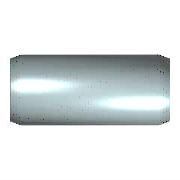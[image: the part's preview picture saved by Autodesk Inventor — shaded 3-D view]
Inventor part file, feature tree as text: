
AUTODESK INVENTOR PART (.ipt)
format: ipt  version: 2023.3 (Build 273359000, 359)  size: 116,224 bytes
history: native  units: mm (DEFAULTED — no unit token found)
features: extrude x1, chamfer x1, sketch x1
ambient origin geometry x8: Origin, YZ Plane, XZ Plane, XY Plane, X Axis, Y Axis, Z Axis, Center Point
bodies: Solid1 (feature_tree)
feature tree (3):
  extrude  "Körper"  Depth=4.0mm
  chamfer  "Skizze2"  [1 undecoded]
  sketch  "Skizze"  dims[d1=1.0mm d2=4.0mm d3=0.0mm d4=0.2mm d5=15.0deg d8=0.2mm d9=15.0deg d11=0.2mm d12=0.2mm d13=0.0mm d15=0.0mm d16=0.0mm]
note: 1 required parameter value undecoded (feature->parameter linkage not recoverable at this tier; creation-order binding heuristic only, values carry confidence <= 0.55)
